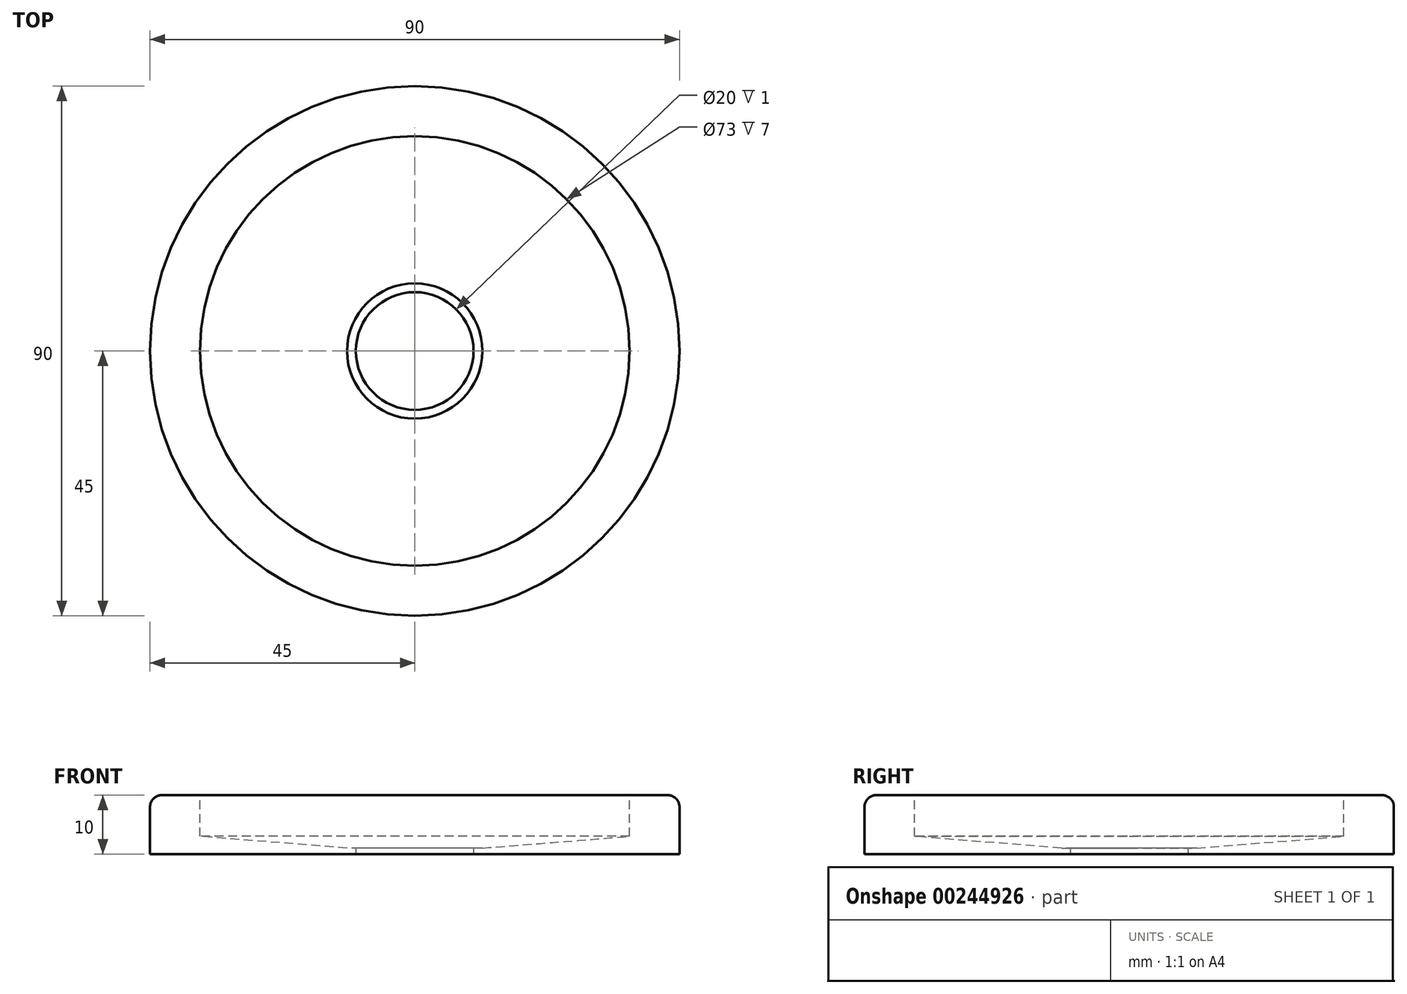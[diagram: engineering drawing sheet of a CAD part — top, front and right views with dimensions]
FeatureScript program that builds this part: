
annotation { "Feature Type Name" : "Feature", "Feature Type Description" : "" }
export const myFeature = defineFeature(function(context is Context, id is Id, definition is map)
    precondition{}
    {
        {
            var Q0;
            Q0=qCreatedBy(makeId("Top.planeOp"),FACE);
            var sketch = newSketch(context, id + "F0", { "sketchPlane" : qUnion([Q0])});
            skCircle(sketch, "E0", {"center": v(0, 0) * mm, "radius": 45 * mm});
            skCircle(sketch, "E1", {"center": v(0, 0) * mm, "radius": 10 * mm});
            skSolve(sketch);
        }
        {
            var Q0;
            Q0 = qSketchRegion(id + "F0", true);
            extrude(context, id + "F1", {"entities" : qUnion([Q0]), "depth" : 10 * mm});
        }
        {
            var Q0;
            Q0=makeQuery(id+"F1.opExtrude","CAP_FACE",FACE,{"disambiguationData":[OSD([sQuery(id+"F0.wireOp",EDGE,"E0"),sQuery(id+"F0.wireOp",EDGE,"E1")])],"isStart":false});
            var sketch = newSketch(context, id + "F2", { "sketchPlane" : qUnion([Q0])});
            skCircle(sketch, "E2", {"center": v(0, 0) * mm, "radius": 36.5 * mm});
            skSolve(sketch);
        }
        {
            var Q0;
            Q0 = qSketchRegion(id + "F2", true);
            extrude(context, id + "F3", {"entities" : qUnion([Q0]), "operationType" : NewBodyOperationType.REMOVE, "oppositeDirection" : true, "depth" : 9 * mm});
        }
        {
            var Q0;
            Q0=makeQuery(id+"F3.boolean.opBoolean","COPY",EDGE,{"derivedFrom":makeQuery(id+"F3.opExtrude","CAP_EDGE",EDGE,{"disambiguationData":[OSD([sQuery(id+"F2.wireOp",EDGE,"E2")])],"isStart":false})});
            chamfer(context, id + "F4", {"entities" : qUnion([Q0]), "chamferType" : ChamferType.TWO_OFFSETS, "width1" : 25 * mm, "oppositeDirection" : false, "width2" : 2 * mm, "tangentPropagation" : true});
        }
        {
            var Q0;
            Q0=makeQuery(id+"F1.opExtrude","CAP_EDGE",EDGE,{"disambiguationData":[OSD([sQuery(id+"F0.wireOp",EDGE,"E0")])],"isStart":false});
            fillet(context, id + "F5", {"entities" : qUnion([Q0]), "radius" : 2 * mm, "tangentPropagation" : true, "allowEdgeOverflow" : false});
        }
    });
